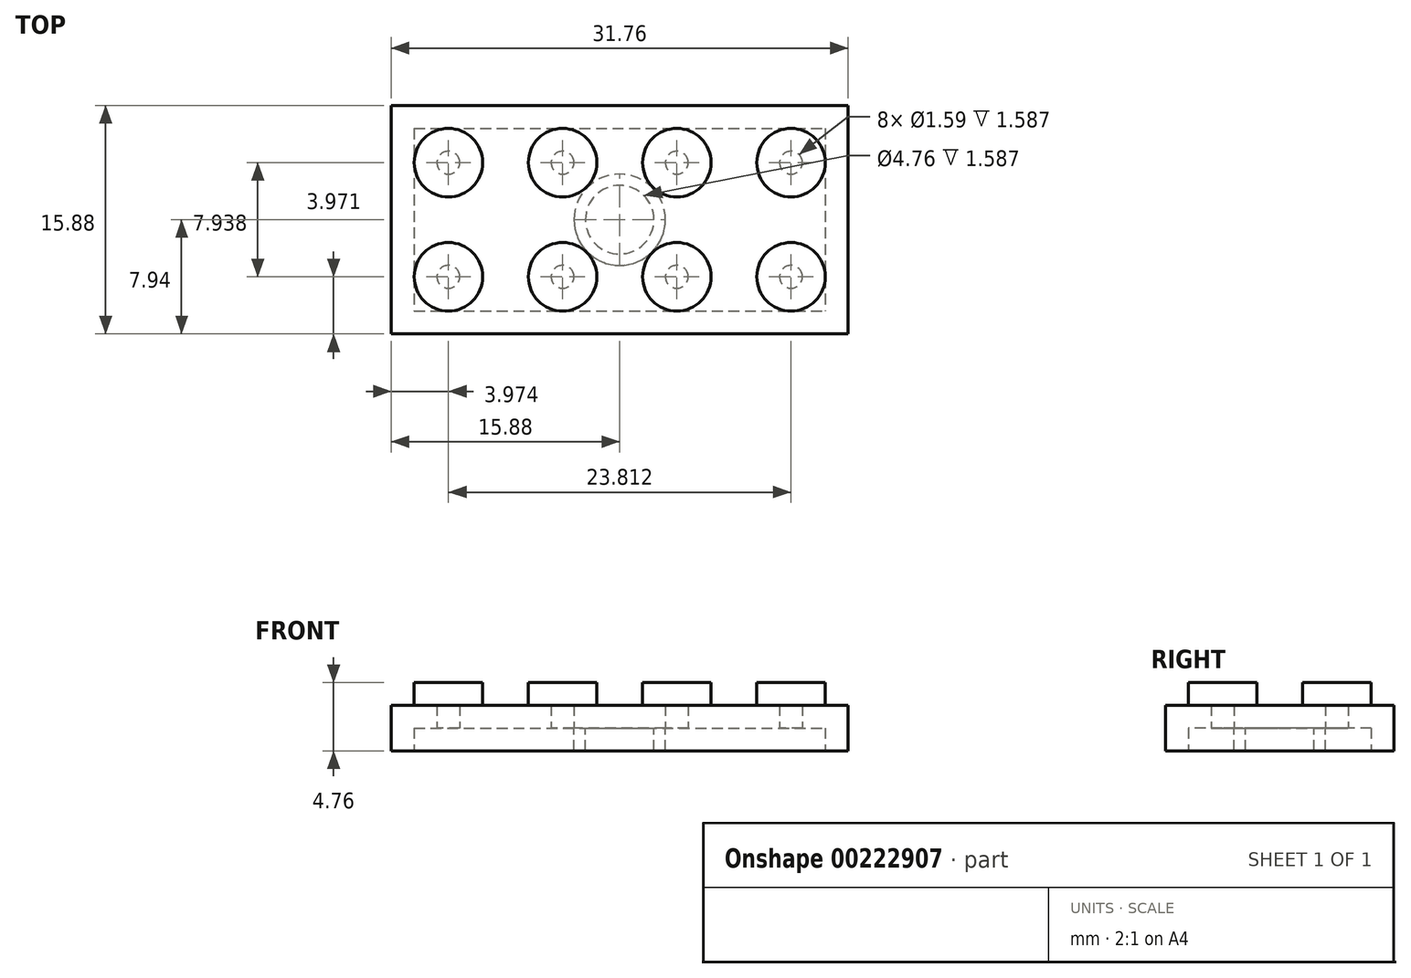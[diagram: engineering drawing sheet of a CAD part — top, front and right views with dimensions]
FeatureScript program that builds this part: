
annotation { "Feature Type Name" : "Feature", "Feature Type Description" : "" }
export const myFeature = defineFeature(function(context is Context, id is Id, definition is map)
    precondition{}
    {
        {
            var Q0;
            Q0=qCreatedBy(makeId("Top.planeOp"),FACE);
            var sketch = newSketch(context, id + "F0", { "sketchPlane" : qUnion([Q0])});
            skLineSegment(sketch, "E0.bottom", {"start": v(-15.88, 7.94) * mm, "end": v(15.88, 7.94) * mm});
            skLineSegment(sketch, "E0.top", {"start": v(-15.88, -7.94) * mm, "end": v(15.88, -7.94) * mm});
            skLineSegment(sketch, "E0.left", {"start": v(-15.88, 7.94) * mm, "end": v(-15.88, -7.94) * mm});
            skLineSegment(sketch, "E0.right", {"start": v(15.88, 7.94) * mm, "end": v(15.88, -7.94) * mm});
            skPoint(sketch, "E0.middle", {"position": v(0, 0) * mm});
            skCircle(sketch, "E1", {"center": v(-11.9, 3.97) * mm, "radius": 2.38 * mm});
            skCircle(sketch, "E2.0.1.0", {"center": v(-11.9, -3.97) * mm, "radius": 2.38 * mm});
            skCircle(sketch, "E2.1.0.0", {"center": v(-3.97, 3.97) * mm, "radius": 2.38 * mm});
            skCircle(sketch, "E2.1.1.0", {"center": v(-3.97, -3.97) * mm, "radius": 2.38 * mm});
            skLineSegment(sketch, "E2.direction1", {"start": v(-11.9, 3.97) * mm, "end": v(-3.97, 3.97) * mm, "construction": true});
            skLineSegment(sketch, "E2.direction2", {"start": v(-11.9, 3.97) * mm, "end": v(-11.9, -3.97) * mm, "construction": true});
            skCircle(sketch, "E3.0.2.0", {"center": v(3.97, 3.97) * mm, "radius": 2.38 * mm});
            skCircle(sketch, "E3.0.2.1", {"center": v(3.97, -3.97) * mm, "radius": 2.38 * mm});
            skCircle(sketch, "E3.0.3.0", {"center": v(11.9, 3.97) * mm, "radius": 2.38 * mm});
            skCircle(sketch, "E3.0.3.1", {"center": v(11.9, -3.97) * mm, "radius": 2.38 * mm});
            skSolve(sketch);
        }
        {
            var Q0;
            Q0=makeQuery(id+"F0.imprint","IMPRINT",FACE,{"disambiguationData":[TD([[makeQuery(id+"F0.imprint","IMPRINT",EDGE,{"derivedFrom":sQuery(id+"F0.wireOp",EDGE,"E0.bottom")}),-1.0]])]});
            extrude(context, id + "F1", {"entities" : qUnion([Q0]), "depth" : 3.17 * mm});
        }
        {
            var Q0;
            Q0=makeQuery(id+"F0.imprint","IMPRINT",FACE,{"disambiguationData":[TD([[makeQuery(id+"F0.imprint","IMPRINT",EDGE,{"derivedFrom":sQuery(id+"F0.wireOp",EDGE,"E1")}),1.0]])]});
            var Q1;
            Q1=makeQuery(id+"F0.imprint","IMPRINT",FACE,{"disambiguationData":[TD([[makeQuery(id+"F0.imprint","IMPRINT",EDGE,{"derivedFrom":sQuery(id+"F0.wireOp",EDGE,"E2.1.0.0")}),1.0]])]});
            var Q2;
            Q2=makeQuery(id+"F0.imprint","IMPRINT",FACE,{"disambiguationData":[TD([[makeQuery(id+"F0.imprint","IMPRINT",EDGE,{"derivedFrom":sQuery(id+"F0.wireOp",EDGE,"E2.1.1.0")}),1.0]])]});
            var Q3;
            Q3=makeQuery(id+"F0.imprint","IMPRINT",FACE,{"disambiguationData":[TD([[makeQuery(id+"F0.imprint","IMPRINT",EDGE,{"derivedFrom":sQuery(id+"F0.wireOp",EDGE,"E2.0.1.0")}),1.0]])]});
            var Q4;
            Q4=makeQuery(id+"F0.imprint","IMPRINT",FACE,{"disambiguationData":[TD([[makeQuery(id+"F0.imprint","IMPRINT",EDGE,{"derivedFrom":sQuery(id+"F0.wireOp",EDGE,"E3.0.2.0")}),1.0]])]});
            var Q5;
            Q5=makeQuery(id+"F0.imprint","IMPRINT",FACE,{"disambiguationData":[TD([[makeQuery(id+"F0.imprint","IMPRINT",EDGE,{"derivedFrom":sQuery(id+"F0.wireOp",EDGE,"E3.0.3.0")}),1.0]])]});
            var Q6;
            Q6=makeQuery(id+"F0.imprint","IMPRINT",FACE,{"disambiguationData":[TD([[makeQuery(id+"F0.imprint","IMPRINT",EDGE,{"derivedFrom":sQuery(id+"F0.wireOp",EDGE,"E3.0.3.1")}),1.0]])]});
            var Q7;
            Q7=makeQuery(id+"F0.imprint","IMPRINT",FACE,{"disambiguationData":[TD([[makeQuery(id+"F0.imprint","IMPRINT",EDGE,{"derivedFrom":sQuery(id+"F0.wireOp",EDGE,"E3.0.2.1")}),1.0]])]});
            extrude(context, id + "F2", {"entities" : qUnion([Q0, Q1, Q2, Q3, Q4, Q5, Q6, Q7]), "operationType" : NewBodyOperationType.ADD, "depth" : 4.76 * mm});
        }
        {
            var Q0;
            {var subQ0=sQuery(id+"F0.wireOp",EDGE,"E2.1.1.0");var subQ1=sQuery(id+"F0.wireOp",EDGE,"E2.1.0.0");var subQ2=sQuery(id+"F0.wireOp",EDGE,"E2.0.1.0");var subQ3=sQuery(id+"F0.wireOp",EDGE,"E1");Q0=makeQuery(id+"F2.boolean.opBoolean","MERGE",FACE,{"derivedFrom":[makeQuery(id+"F1.opExtrude","CAP_FACE",FACE,{"disambiguationData":[OSD([sQuery(id+"F0.wireOp",EDGE,"E0.bottom"),sQuery(id+"F0.wireOp",EDGE,"E0.top"),sQuery(id+"F0.wireOp",EDGE,"E0.left"),sQuery(id+"F0.wireOp",EDGE,"E0.right"),subQ3,subQ2,subQ1,subQ0])],"isStart":true}),makeQuery(id+"F2.opExtrude","CAP_FACE",FACE,{"disambiguationData":[OSD([subQ3])],"isStart":true}),makeQuery(id+"F2.opExtrude","CAP_FACE",FACE,{"disambiguationData":[OSD([subQ2])],"isStart":true}),makeQuery(id+"F2.opExtrude","CAP_FACE",FACE,{"disambiguationData":[OSD([subQ1])],"isStart":true}),makeQuery(id+"F2.opExtrude","CAP_FACE",FACE,{"disambiguationData":[OSD([subQ0])],"isStart":true})]});}
            shell(context, id + "F3", {"entities" : qUnion([Q0]), "thickness" : 1.59 * mm});
        }
        {
            var Q0;
            Q0=makeQuery(id+"F3.opShell","OFFSET_FACE",FACE,{"disambiguationData":[OSD([sQuery(id+"F0.wireOp",EDGE,"E0.bottom"),sQuery(id+"F0.wireOp",EDGE,"E0.top"),sQuery(id+"F0.wireOp",EDGE,"E0.left"),sQuery(id+"F0.wireOp",EDGE,"E0.right"),sQuery(id+"F0.wireOp",EDGE,"E1"),sQuery(id+"F0.wireOp",EDGE,"E2.0.1.0"),sQuery(id+"F0.wireOp",EDGE,"E2.1.0.0"),sQuery(id+"F0.wireOp",EDGE,"E2.1.1.0")])]});
            var sketch = newSketch(context, id + "F4", { "sketchPlane" : qUnion([Q0])});
            skCircle(sketch, "E4", {"center": v(0, 0) * mm, "radius": 3.18 * mm});
            skCircle(sketch, "E5", {"center": v(0, 0) * mm, "radius": 2.38 * mm});
            skSolve(sketch);
        }
        {
            var Q0;
            Q0=makeQuery(id+"F4.imprint","IMPRINT",FACE,{"disambiguationData":[TD([[makeQuery(id+"F4.imprint","IMPRINT",EDGE,{"derivedFrom":sQuery(id+"F4.wireOp",EDGE,"E4")}),1.0]])]});
            extrude(context, id + "F5", {"entities" : qUnion([Q0]), "operationType" : NewBodyOperationType.ADD, "depth" : 1.59 * mm});
        }
    });
